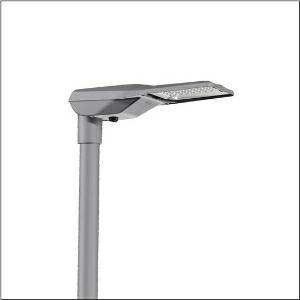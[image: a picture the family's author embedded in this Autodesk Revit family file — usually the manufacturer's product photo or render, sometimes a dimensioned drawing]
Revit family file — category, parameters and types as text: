
# Revit family: streetlight_sl_21_iq_mini___st1_0a_5xe2d31u08gb_76f1
name_source: partatom
category: Lighting Fixtures
units: mm (PartAtom-declared; Revit-internal decimal feet)

## family parameters
Cut with Voids When Loaded = No
Host = Face
Light Source = No
Part Type = Normal
Room Calculation Point = No
Round Connector Dimension = Use Diameter
Shared = No

## types (1)
- --- (1 x LED, 5990 lm, 39.8 W, 3000K)
    Apparent Load = 40 VA
    CIE Flux Codes = 37 72 97 100 100
    Color Rendering = 70
    Color Temperature = 3000K
    Default Elevation = 1800 mm
    Description = Streetlight SL 21 iQ mini, mast luminaire, primary light control with lens, of PMMA, primary optical cover: cover, of toughened safety glass, transparent, light distribution: ST1.0a, light emission: direct distribution, primary light characteristic: asymmetric, installation type: post-top, side-entry, LED, High Power LED, rated luminous flux: 5.990lm, luminous efficacy: 151lm/W, light colour: 730, colour temperature: 3000K, control gear: iQ-Street Remote, D4i with power reduction, control: pre-setting: logarithmic dimming characteristic, Street-Remote, Auto-Match, Temp-Guard, Lumen-Switch, Night-Set, Smart-Wire, Light-Fading, Desk-Remote (wireless, voltage-free reading and setting of iQ features in the workshop via application-optimized NFC function/RFID function), optimised constant luminous flux control (CLO 2.0), mains connection: 220..240V, AC, 50/60Hz, start of lifetime: 40W, end of service life: 41W, reduction: 18W, luminaire housing, of diecast aluminium, powder-coated, Siteco® metallic grey (DB 702S), corrosivity category C5 mid according to DIN EN ISO 12944, please order mast flange separately, inclination adjustable: 0°, 5°, 10°, 15°, sealing non-destructively replaceable, multi-level sealing system, length: 628mm, width: 235mm, height: 110mm, mast flange for spigot size: 42mm (side-entry): 5XC10008XM4, 60/48mm (side-entry/post-top): 5XC10108XM2, 76/60mm (side-entry/post-top): 5XC10108XM1, mounting height: 4..8m, Smart Interface below, protection rating (complete): IP66, insulation class (complete): insulation class II (safety insulation), certification: CE, ENEC, ENEC+, VDE, impact resistance: IK10, permissible operating ambient temperature for outdoor applications: -40..+50°C, standard-compliant lighting for roads and squares, packaging unit: 1 piece

Light Distribution: ST1.0a
    Height = 110 mm
    Lamp = 1 x LED
    Lamp Light Flux = 5990 lm
    Lamp Power = 39.8 W
    Lamp count = 1
    Length = 625 mm
    Luminous efficacy = 151 lm/W
    Manufacturer = Siteco
    ModVariant = No
    Model = 5XE2D31U08GB
    Number of Poles = 1
    OnlyDefault = Yes
    Power Factor = 1
    Product Name = Streetlight SL 21 iQ mini | ST1.0a
    Product group = mast luminaire | pylon top
    ProductGroupID = 6100
    Protection Class = Protection class II
    Protection Degree = IP 66
    RLX_Detail_Level = 1
    RLX_Emergency_Light_Flux = 0 lm
    RLX_Emergency_Type = 0
    RLX_Emergency_Type_DB = No
    RlxData = <blob elided: 92769 chars, md5=a3e0909a>
    Socket = socket
    Standby Power = 0 W
    System Light Flux = 5990 lm
    System Power = 40 W
    Type Comments = factory setting: luminous flux: 100 % | dim-lin: 254 | 800 mA
    Type Image = l_1003516.jpg
    URL = http://relux.com
    VarID = @adj_136703
    Voltage = 0 V
    Weight = 0.00 kg
    Width = 234 mm

## geometry (parser evidence)
native form markers: Blend x4, Sweep x11
no freeform markers — native parametric forms only
